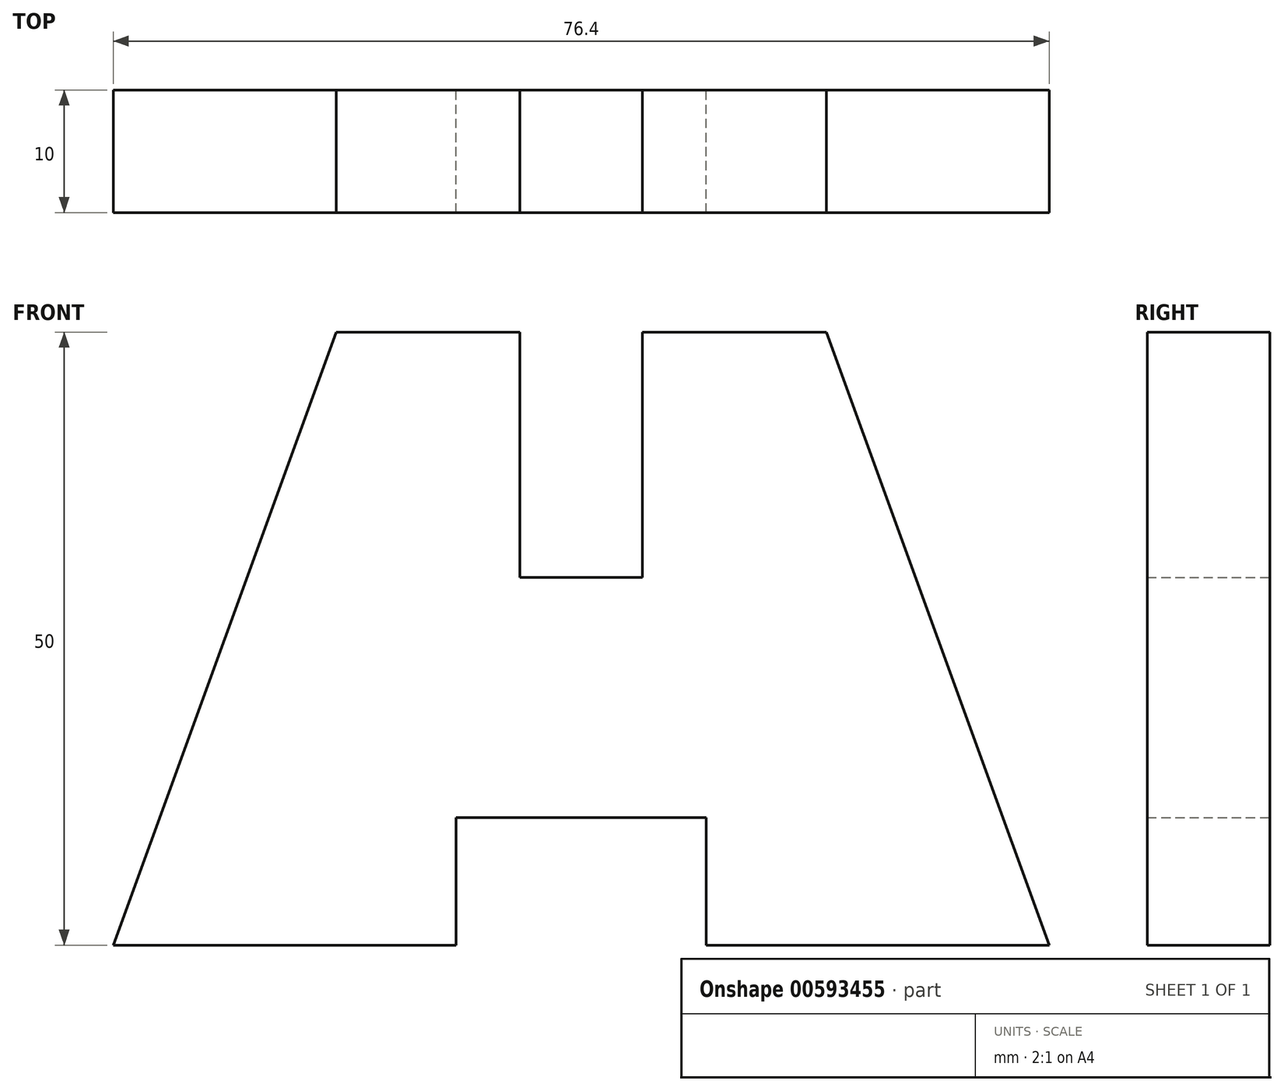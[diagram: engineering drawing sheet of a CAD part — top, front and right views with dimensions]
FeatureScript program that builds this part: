
annotation { "Feature Type Name" : "Feature", "Feature Type Description" : "" }
export const myFeature = defineFeature(function(context is Context, id is Id, definition is map)
    precondition{}
    {
        {
            var Q0;
            Q0=qCreatedBy(makeId("Front.planeOp"),FACE);
            var sketch = newSketch(context, id + "F0", { "sketchPlane" : qUnion([Q0])});
            skLineSegment(sketch, "E0", {"start": v(-38.2, 0) * mm, "end": v(-20, 50) * mm});
            skLineSegment(sketch, "E1", {"start": v(-20, 50) * mm, "end": v(-5, 50) * mm});
            skLineSegment(sketch, "E2", {"start": v(-5, 50) * mm, "end": v(-5, 30) * mm});
            skLineSegment(sketch, "E3", {"start": v(-5, 30) * mm, "end": v(5, 30) * mm});
            skLineSegment(sketch, "E4", {"start": v(5, 30) * mm, "end": v(5, 50) * mm});
            skLineSegment(sketch, "E5", {"start": v(5, 50) * mm, "end": v(20, 50) * mm});
            skLineSegment(sketch, "E6", {"start": v(20, 50) * mm, "end": v(38.2, 0) * mm});
            skLineSegment(sketch, "E7", {"start": v(38.2, 0) * mm, "end": v(10.2, 0) * mm});
            skLineSegment(sketch, "E8", {"start": v(10.2, 0) * mm, "end": v(10.2, 10.4) * mm});
            skLineSegment(sketch, "E9", {"start": v(10.2, 10.4) * mm, "end": v(-10.2, 10.4) * mm});
            skLineSegment(sketch, "E10", {"start": v(-10.2, 10.4) * mm, "end": v(-10.2, 0) * mm});
            skLineSegment(sketch, "E11", {"start": v(-10.2, 0) * mm, "end": v(-38.2, 0) * mm});
            skSolve(sketch);
        }
        {
            var Q0;
            Q0=makeQuery(id+"F0.imprint","IMPRINT",FACE,{"disambiguationData":[TD([[makeQuery(id+"F0.imprint","IMPRINT",EDGE,{"derivedFrom":sQuery(id+"F0.wireOp",EDGE,"E0")}),-1.0]])]});
            extrude(context, id + "F1", {"entities" : qUnion([Q0]), "depth" : 10 * mm, "offsetDistance" : 25.4 * mm});
        }
    });
